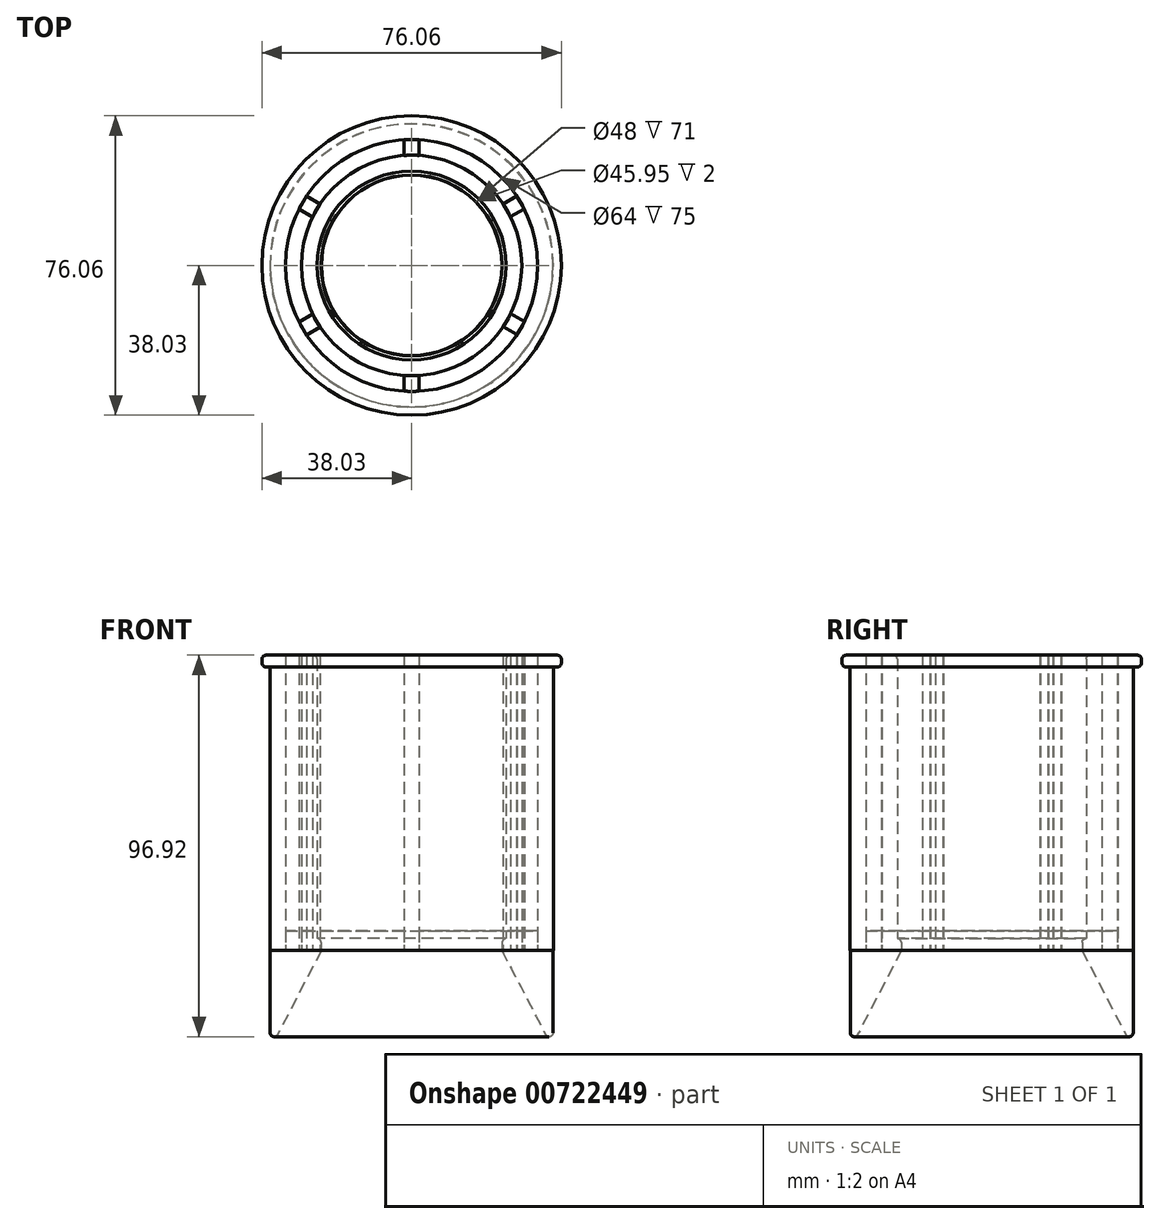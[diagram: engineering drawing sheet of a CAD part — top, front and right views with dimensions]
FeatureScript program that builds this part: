
annotation { "Feature Type Name" : "Feature", "Feature Type Description" : "" }
export const myFeature = defineFeature(function(context is Context, id is Id, definition is map)
    precondition{}
    {
        {
            var Q0;
            Q0=qCreatedBy(makeId("Top.planeOp"),FACE);
            var sketch = newSketch(context, id + "F0", { "sketchPlane" : qUnion([Q0])});
            skCircle(sketch, "E0", {"center": v(0, 0) * mm, "radius": 24 * mm});
            skCircle(sketch, "E1", {"center": v(0, 0) * mm, "radius": 28 * mm});
            skCircle(sketch, "E2", {"center": v(0, 0) * mm, "radius": 32 * mm});
            skCircle(sketch, "E3", {"center": v(0, 0) * mm, "radius": 36 * mm});
            skCircle(sketch, "E4", {"center": v(0, 0) * mm, "radius": 22.98 * mm});
            skLineSegment(sketch, "E5", {"start": v(-1.94, 31.94) * mm, "end": v(-1.94, 27.93) * mm});
            skLineSegment(sketch, "E6", {"start": v(1.87, 31.95) * mm, "end": v(1.87, 27.94) * mm});
            skSolve(sketch);
        }
        {
            var Q0;
            Q0=makeQuery(id+"F0.imprint","IMPRINT",FACE,{"disambiguationData":[TD([[makeQuery(id+"F0.imprint","IMPRINT",EDGE,{"derivedFrom":sQuery(id+"F0.wireOp",EDGE,"E0")}),-1.0]])]});
            var Q1;
            Q1=makeQuery(id+"F0.imprint","IMPRINT",FACE,{"disambiguationData":[TD([[makeQuery(id+"F0.imprint","IMPRINT",EDGE,{"derivedFrom":sQuery(id+"F0.wireOp",EDGE,"E3")}),1.0]])]});
            extrude(context, id + "F1", {"entities" : qUnion([Q0, Q1]), "depth" : 75 * mm, "offsetDistance" : 25 * mm});
        }
        {
            var Q0;
            {var subQ0=sQuery(id+"F0.wireOp",EDGE,"E5");Q0=makeQuery(id+"F0.imprint","IMPRINT",FACE,{"disambiguationData":[TD([[makeQuery(id+"F0.imprint","IMPRINT",EDGE,{"derivedFrom":subQ0}),1.0]])]});}
            extrude(context, id + "F2", {"entities" : qUnion([Q0]), "depth" : 75 * mm, "offsetDistance" : 25 * mm});
        }
        {
            var Q0;
            {var subQ0=sQuery(id+"F0.wireOp",EDGE,"E5");Q0=makeQuery(id+"F0.imprint","IMPRINT",FACE,{"disambiguationData":[TD([[makeQuery(id+"F0.imprint","IMPRINT",EDGE,{"derivedFrom":subQ0}),-1.0]])]});}
            extrude(context, id + "F3", {"entities" : qUnion([Q0]), "depth" : 5 * mm, "offsetDistance" : 25 * mm});
        }
        {
            var Q0;
            Q0=makeQuery(id+"F0.imprint","IMPRINT",FACE,{"disambiguationData":[TD([[makeQuery(id+"F0.imprint","IMPRINT",EDGE,{"derivedFrom":sQuery(id+"F0.wireOp",EDGE,"E0")}),1.0]])]});
            extrude(context, id + "F4", {"entities" : qUnion([Q0]), "operationType" : NewBodyOperationType.ADD, "depth" : 3 * mm, "offsetDistance" : 25 * mm});
        }
        {
            var Q0;
            Q0=qCreatedBy(makeId("Right.planeOp"),FACE);
            var sketch = newSketch(context, id + "F5", { "sketchPlane" : qUnion([Q0])});
            skLineSegment(sketch, "E7", {"start": v(22.92, 0) * mm, "end": v(35.93, -25.01) * mm});
            skLineSegment(sketch, "E8", {"start": v(35.93, -25.01) * mm, "end": v(35.93, 0) * mm});
            skLineSegment(sketch, "E9", {"start": v(35.93, 0) * mm, "end": v(22.92, 0) * mm});
            skSolve(sketch);
        }
        {
            var Q0;
            Q0=qCreatedBy(makeId("Right.planeOp"),FACE);
            var sketch = newSketch(context, id + "F6", { "sketchPlane" : qUnion([Q0])});
            skLineSegment(sketch, "E10", {"start": v(0, 0) * mm, "end": v(0, -38.6) * mm});
            skLineSegment(sketch, "E11", {"start": v(0, 0) * mm, "end": v(0, 90.49) * mm});
            skSolve(sketch);
        }
        {
            var Q0;
            Q0=makeQuery(id+"F5.imprint","IMPRINT",FACE,{"disambiguationData":[TD([[makeQuery(id+"F5.imprint","IMPRINT",EDGE,{"derivedFrom":sQuery(id+"F5.wireOp",EDGE,"E7")}),1.0]])]});
            var Q1;
            Q1=sQuery(id+"F6.wireOp",EDGE,"E10");
            revolve(context, id + "F7", {"surfaceOperationType" : NewSurfaceOperationType.NEW, "entities" : qUnion([Q0]), "axis" : qUnion([Q1]), "revolveType" : RevolveType.FULL});
        }
        {
            var Q0;
            Q0=makeQuery(id+"F2.opExtrude","SWEPT_BODY",BODY,{"disambiguationData":[OSD([sQuery(id+"F0.wireOp",EDGE,"E1"),sQuery(id+"F0.wireOp",EDGE,"E2"),sQuery(id+"F0.wireOp",EDGE,"E5"),sQuery(id+"F0.wireOp",EDGE,"E6")])]});
            var Q1;
            Q1=sQuery(id+"F6.wireOp",EDGE,"E11");
            circularPattern(context, id + "F8", {"entities" : qUnion([Q0]), "axis" : qUnion([Q1]), "angle" : 360 * degree, "instanceCount" : 6, "equalSpace" : true});
        }
        {
            var Q0;
            Q0=makeQuery(id+"F1.opExtrude","CAP_FACE",FACE,{"disambiguationData":[OSD([sQuery(id+"F0.wireOp",EDGE,"E2"),sQuery(id+"F0.wireOp",EDGE,"E3")])],"isStart":false});
            var sketch = newSketch(context, id + "F9", { "sketchPlane" : qUnion([Q0])});
            skCircle(sketch, "E12", {"center": v(0, 0) * mm, "radius": 38.03 * mm});
            skSolve(sketch);
        }
        {
            var Q0;
            Q0=makeQuery(id+"F9.imprint","IMPRINT",FACE,{"disambiguationData":[TD([[makeQuery(id+"F9.imprint","IMPRINT",EDGE,{"derivedFrom":sQuery(id+"F9.wireOp",EDGE,"E12")}),1.0]])]});
            extrude(context, id + "F10", {"entities" : qUnion([Q0]), "operationType" : NewBodyOperationType.ADD, "depth" : -3 * mm, "offsetDistance" : 25 * mm});
        }
        {
            var Q0;
            Q0=makeQuery(id+"F7.opRevolve","SWEPT_EDGE",EDGE,{"disambiguationData":[OSD([sQuery(id+"F5.wireOp",EDGE,"E7"),sQuery(id+"F5.wireOp",EDGE,"E8")])]});
            var Q1;
            Q1=makeQuery(id+"F10.opExtrude","CAP_EDGE",EDGE,{"disambiguationData":[OSD([sQuery(id+"F9.wireOp",EDGE,"E12")])],"isStart":true});
            var Q2;
            Q2=makeQuery(id+"F1.opExtrude","CAP_EDGE",EDGE,{"disambiguationData":[OSD([sQuery(id+"F0.wireOp",EDGE,"E0")])],"isStart":false});
            var Q3;
            Q3=makeQuery(id+"F10.opExtrude","CAP_EDGE",EDGE,{"disambiguationData":[OSD([sQuery(id+"F0.wireOp",EDGE,"E3")])],"isStart":false});
            var Q4;
            Q4=makeQuery(id+"F10.opExtrude","CAP_EDGE",EDGE,{"disambiguationData":[OSD([sQuery(id+"F9.wireOp",EDGE,"E12")])],"isStart":false});
            var Q5;
            Q5=makeQuery(id+"F4.opExtrude","CAP_EDGE",EDGE,{"disambiguationData":[OSD([sQuery(id+"F0.wireOp",EDGE,"E4")])],"isStart":false});
            fillet(context, id + "F11", {"entities" : qUnion([Q0, Q1, Q2, Q3, Q4, Q5]), "radius" : 1 * mm, "tangentPropagation" : true, "allowEdgeOverflow" : false});
        }
    });
